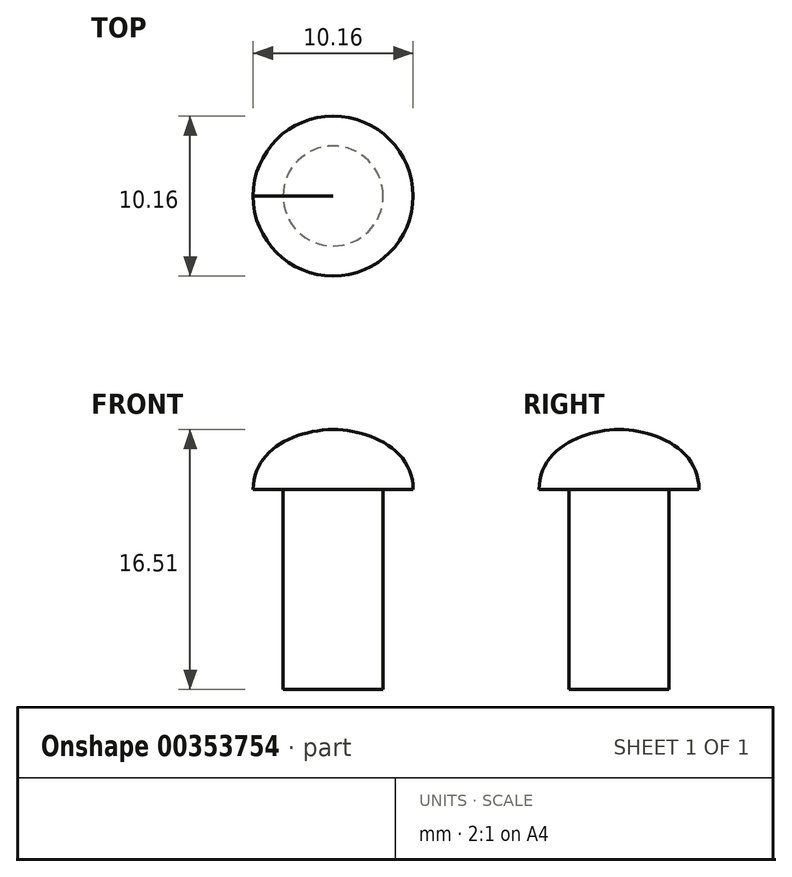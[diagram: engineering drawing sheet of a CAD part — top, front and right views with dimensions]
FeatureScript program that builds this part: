
annotation { "Feature Type Name" : "Feature", "Feature Type Description" : "" }
export const myFeature = defineFeature(function(context is Context, id is Id, definition is map)
    precondition{}
    {
        {
            var Q0;
            Q0=qCreatedBy(makeId("Front.planeOp"),FACE);
            var sketch = newSketch(context, id + "F0", { "sketchPlane" : qUnion([Q0])});
            skLineSegment(sketch, "E0.bottom", {"start": v(-3.18, -6.35) * mm, "end": v(3.17, -6.35) * mm});
            skLineSegment(sketch, "E0.top", {"start": v(-3.18, 6.35) * mm, "end": v(3.17, 6.35) * mm});
            skLineSegment(sketch, "E0.left", {"start": v(-3.18, -6.35) * mm, "end": v(-3.18, 6.35) * mm});
            skLineSegment(sketch, "E0.right", {"start": v(3.18, -6.35) * mm, "end": v(3.17, 6.35) * mm});
            skPoint(sketch, "E0.middle", {"position": v(0, 0) * mm});
            skLineSegment(sketch, "E1", {"start": v(-3.18, 6.35) * mm, "end": v(-5.08, 6.35) * mm});
            skLineSegment(sketch, "E2", {"start": v(3.17, 6.35) * mm, "end": v(5.08, 6.35) * mm});
            skFitSpline(sketch, "E3", {"points": [v(-5.08, 6.35) * mm, v(5.08, 6.35) * mm], "startDerivative": vector(0, 14.55) * mm, "endDerivative": vector(0.42, -15.92) * mm});
            skPoint(sketch, "E4", {"position": v(0, 10.16) * mm});
            skLineSegment(sketch, "E5", {"start": v(0, 10.16) * mm, "end": v(0, -6.35) * mm});
            skSolve(sketch);
        }
        {
            var Q0;
            {var subQ0=sQuery(id+"F0.wireOp",EDGE,"E0.left");Q0=makeQuery(id+"F0.imprint","IMPRINT",FACE,{"disambiguationData":[TD([[makeQuery(id+"F0.imprint","IMPRINT",EDGE,{"derivedFrom":subQ0}),-1.0]])]});}
            var Q1;
            {var subQ0=sQuery(id+"F0.wireOp",EDGE,"E1");Q1=makeQuery(id+"F0.imprint","IMPRINT",FACE,{"disambiguationData":[TD([[makeQuery(id+"F0.imprint","IMPRINT",EDGE,{"derivedFrom":subQ0}),-1.0]])]});}
            var Q2;
            Q2=sQuery(id+"F0.wireOp",EDGE,"E5");
            revolve(context, id + "F1", {"entities" : qUnion([Q0, Q1]), "axis" : qUnion([Q2]), "revolveType" : RevolveType.FULL});
        }
    });
